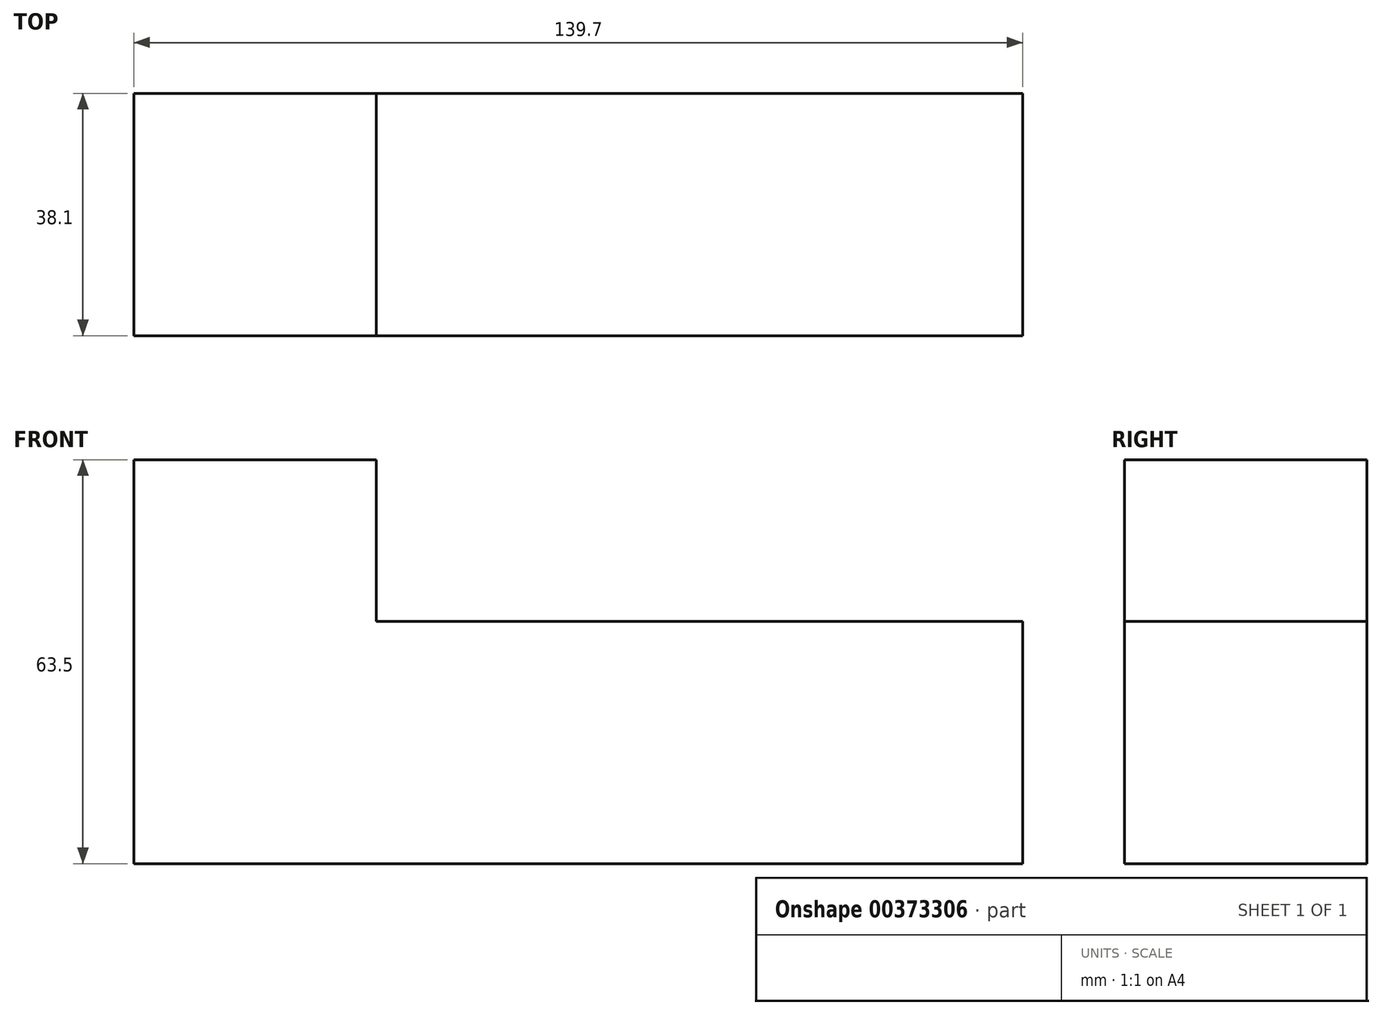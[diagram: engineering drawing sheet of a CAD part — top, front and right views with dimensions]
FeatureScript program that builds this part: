
annotation { "Feature Type Name" : "Feature", "Feature Type Description" : "" }
export const myFeature = defineFeature(function(context is Context, id is Id, definition is map)
    precondition{}
    {
        {
            var Q0;
            Q0=qCreatedBy(makeId("Front.planeOp"),FACE);
            var sketch = newSketch(context, id + "F0", { "sketchPlane" : qUnion([Q0])});
            skLineSegment(sketch, "E0", {"start": v(-97.61, 57.16) * mm, "end": v(-97.61, -6.34) * mm});
            skLineSegment(sketch, "E1", {"start": v(-97.61, -6.34) * mm, "end": v(42.09, -6.34) * mm});
            skLineSegment(sketch, "E2", {"start": v(42.09, -6.34) * mm, "end": v(42.09, 31.76) * mm});
            skLineSegment(sketch, "E3", {"start": v(42.09, 31.76) * mm, "end": v(-59.51, 31.76) * mm});
            skLineSegment(sketch, "E4", {"start": v(-59.51, 31.76) * mm, "end": v(-59.51, 57.16) * mm});
            skLineSegment(sketch, "E5", {"start": v(-59.51, 57.16) * mm, "end": v(-97.61, 57.16) * mm});
            skSolve(sketch);
        }
        {
            var Q0;
            Q0=makeQuery(id+"F0.imprint","IMPRINT",FACE,{"disambiguationData":[TD([[makeQuery(id+"F0.imprint","IMPRINT",EDGE,{"derivedFrom":sQuery(id+"F0.wireOp",EDGE,"E0")}),1.0]])]});
            extrude(context, id + "F1", {"entities" : qUnion([Q0]), "depth" : 38.1 * mm});
        }
    });
